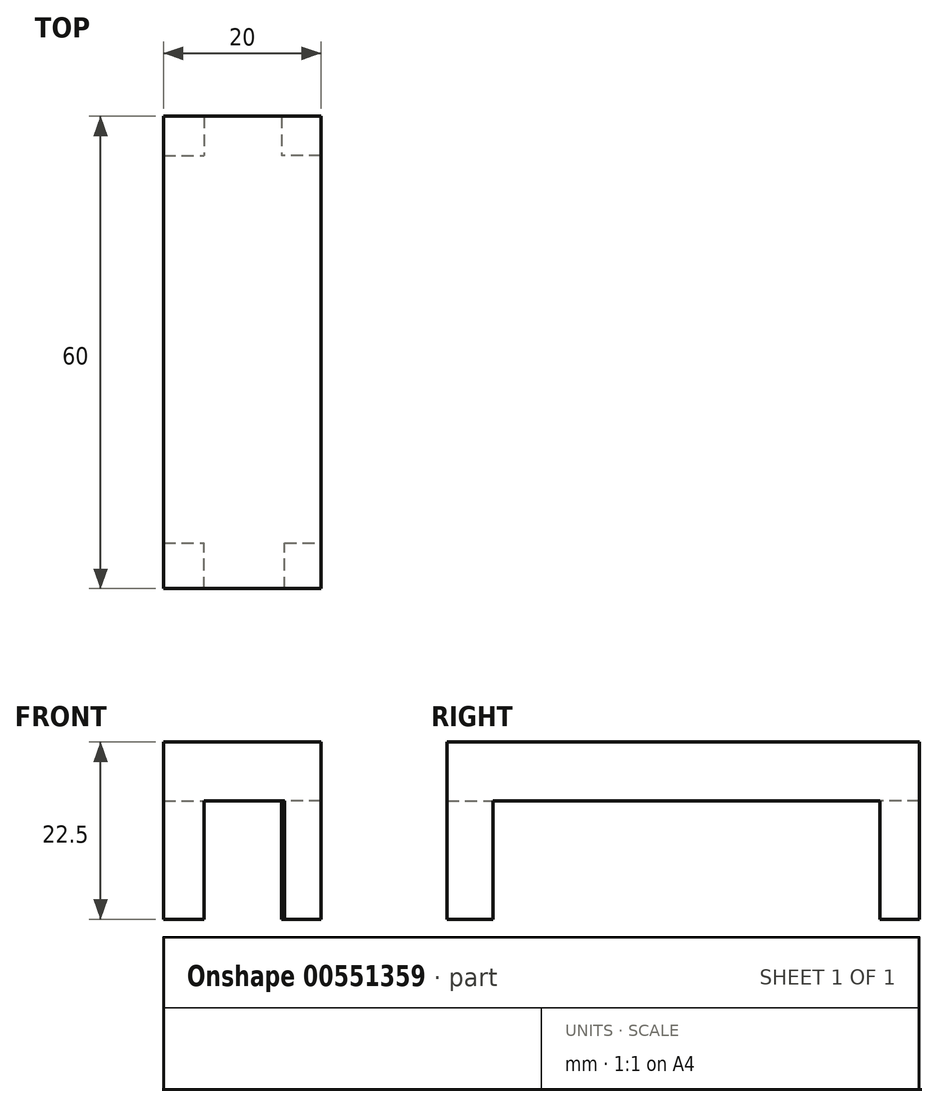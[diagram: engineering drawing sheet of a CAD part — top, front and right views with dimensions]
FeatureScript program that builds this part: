
annotation { "Feature Type Name" : "Feature", "Feature Type Description" : "" }
export const myFeature = defineFeature(function(context is Context, id is Id, definition is map)
    precondition{}
    {
        {
            var Q0;
            Q0=qCreatedBy(makeId("Top.planeOp"),FACE);
            var sketch = newSketch(context, id + "F0", { "sketchPlane" : qUnion([Q0])});
            skLineSegment(sketch, "E0.bottom", {"start": v(-5.12, 41.94) * mm, "end": v(14.88, 41.94) * mm});
            skLineSegment(sketch, "E0.top", {"start": v(-5.12, -18.06) * mm, "end": v(14.88, -18.06) * mm});
            skLineSegment(sketch, "E0.left", {"start": v(-5.12, 41.94) * mm, "end": v(-5.12, -18.06) * mm});
            skLineSegment(sketch, "E0.right", {"start": v(14.88, 41.94) * mm, "end": v(14.88, -18.06) * mm});
            skSolve(sketch);
        }
        {
            var Q0;
            Q0 = qSketchRegion(id + "F0", true);
            extrude(context, id + "F1", {"entities" : qUnion([Q0]), "depth" : 7.5 * mm, "offsetDistance" : 25 * mm});
        }
        {
            var Q0;
            Q0=makeQuery(id+"F1.opExtrude","CAP_FACE",FACE,{"disambiguationData":[OSD([sQuery(id+"F0.wireOp",EDGE,"E0.bottom"),sQuery(id+"F0.wireOp",EDGE,"E0.top"),sQuery(id+"F0.wireOp",EDGE,"E0.left"),sQuery(id+"F0.wireOp",EDGE,"E0.right")])],"isStart":true});
            var sketch = newSketch(context, id + "F2", { "sketchPlane" : qUnion([Q0])});
            skLineSegment(sketch, "E1.bottom", {"start": v(-5.12, 18.06) * mm, "end": v(0, 18.06) * mm});
            skLineSegment(sketch, "E1.top", {"start": v(-5.12, 12.25) * mm, "end": v(0, 12.25) * mm});
            skLineSegment(sketch, "E1.left", {"start": v(-5.12, 18.06) * mm, "end": v(-5.12, 12.25) * mm});
            skLineSegment(sketch, "E1.right", {"start": v(0, 18.06) * mm, "end": v(0, 12.25) * mm});
            skLineSegment(sketch, "E2.bottom", {"start": v(10.26, 18.06) * mm, "end": v(14.88, 18.06) * mm});
            skLineSegment(sketch, "E2.top", {"start": v(10.26, 12.25) * mm, "end": v(14.88, 12.25) * mm});
            skLineSegment(sketch, "E2.left", {"start": v(10.26, 18.06) * mm, "end": v(10.26, 12.25) * mm});
            skLineSegment(sketch, "E2.right", {"start": v(14.88, 18.06) * mm, "end": v(14.88, 12.25) * mm});
            skLineSegment(sketch, "E3.bottom", {"start": v(14.88, -41.94) * mm, "end": v(9.88, -41.94) * mm});
            skLineSegment(sketch, "E3.top", {"start": v(14.88, -36.94) * mm, "end": v(9.88, -36.94) * mm});
            skLineSegment(sketch, "E3.left", {"start": v(14.88, -41.94) * mm, "end": v(14.88, -36.94) * mm});
            skLineSegment(sketch, "E3.right", {"start": v(9.88, -41.94) * mm, "end": v(9.88, -36.94) * mm});
            skLineSegment(sketch, "E4.bottom", {"start": v(-5.12, -41.94) * mm, "end": v(0, -41.94) * mm});
            skLineSegment(sketch, "E4.top", {"start": v(-5.12, -36.94) * mm, "end": v(0, -36.94) * mm});
            skLineSegment(sketch, "E4.left", {"start": v(-5.12, -41.94) * mm, "end": v(-5.12, -36.94) * mm});
            skLineSegment(sketch, "E4.right", {"start": v(0, -41.94) * mm, "end": v(0, -36.94) * mm});
            skSolve(sketch);
        }
        {
            var Q0;
            Q0 = qSketchRegion(id + "F2", true);
            extrude(context, id + "F3", {"entities" : qUnion([Q0]), "operationType" : NewBodyOperationType.ADD, "depth" : 15 * mm, "offsetDistance" : 25 * mm});
        }
    });
